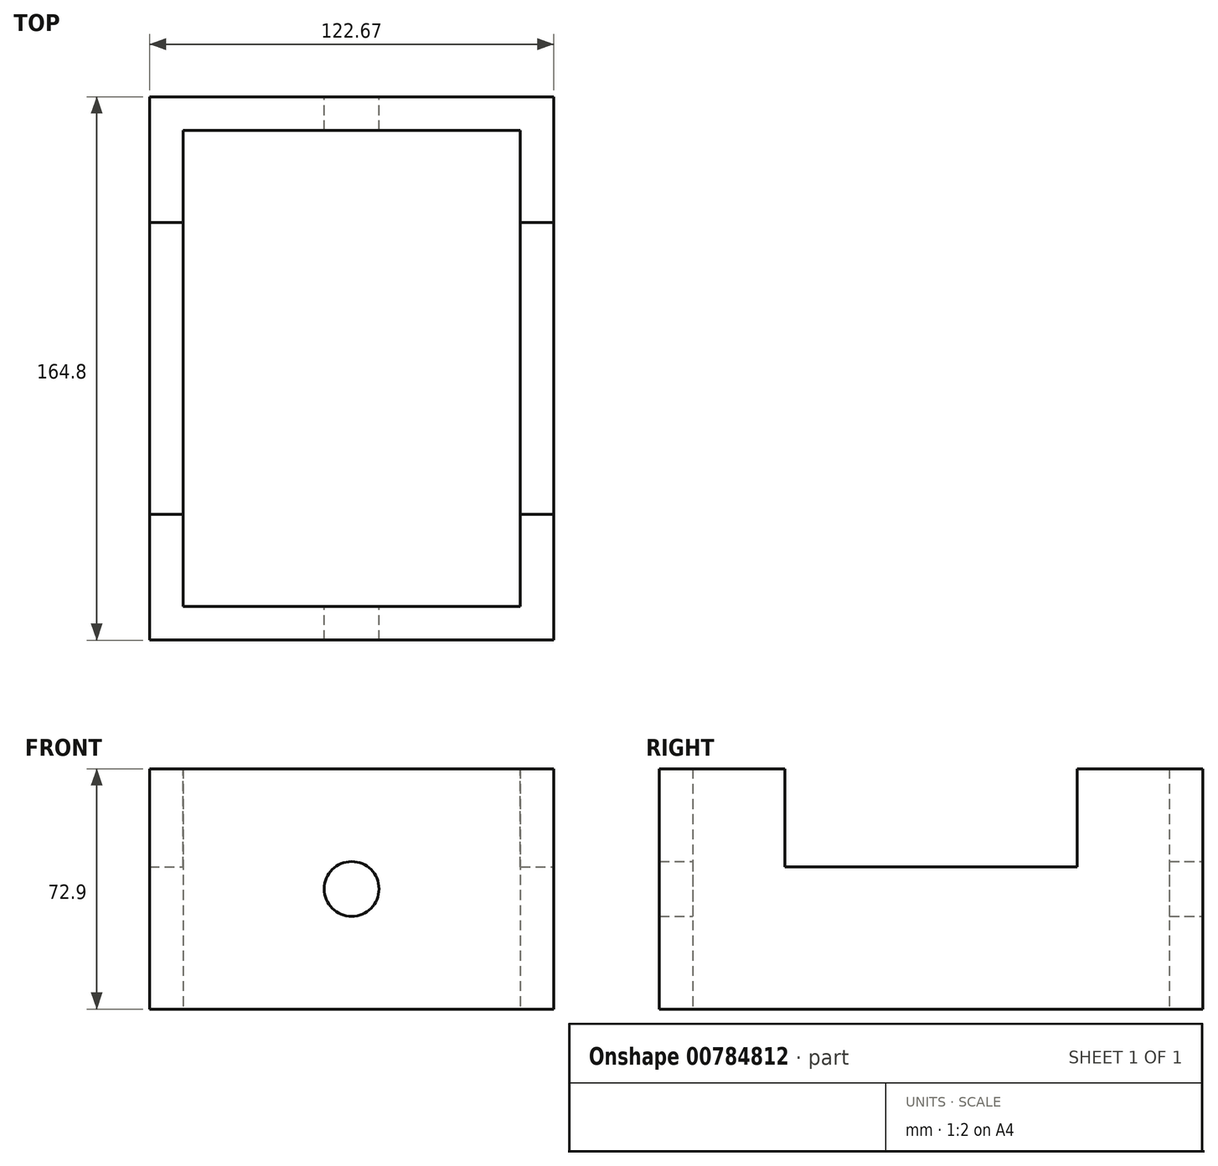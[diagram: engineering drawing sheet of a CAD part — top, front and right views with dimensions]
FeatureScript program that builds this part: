
annotation { "Feature Type Name" : "Feature", "Feature Type Description" : "" }
export const myFeature = defineFeature(function(context is Context, id is Id, definition is map)
    precondition{}
    {
        {
            var Q0;
            Q0=qCreatedBy(makeId("Top.planeOp"),FACE);
            var sketch = newSketch(context, id + "F0", { "sketchPlane" : qUnion([Q0])});
            skLineSegment(sketch, "E0.bottom", {"start": v(-84.1, 82.4) * mm, "end": v(38.56, 82.4) * mm});
            skLineSegment(sketch, "E0.top", {"start": v(-84.1, -82.4) * mm, "end": v(38.56, -82.4) * mm});
            skLineSegment(sketch, "E0.left", {"start": v(-84.1, 82.4) * mm, "end": v(-84.1, -82.4) * mm});
            skLineSegment(sketch, "E0.right", {"start": v(38.56, 82.4) * mm, "end": v(38.56, -82.4) * mm});
            skLineSegment(sketch, "E1.bottom", {"start": v(-73.95, 72.24) * mm, "end": v(28.4, 72.24) * mm});
            skLineSegment(sketch, "E1.top", {"start": v(-73.95, -72.24) * mm, "end": v(28.4, -72.24) * mm});
            skLineSegment(sketch, "E1.left", {"start": v(-73.95, 72.24) * mm, "end": v(-73.95, -72.24) * mm});
            skLineSegment(sketch, "E1.right", {"start": v(28.4, 72.24) * mm, "end": v(28.4, -72.24) * mm});
            skSolve(sketch);
        }
        {
            var Q0;
            Q0=makeQuery(id+"F0.imprint","IMPRINT",FACE,{"disambiguationData":[TD([[makeQuery(id+"F0.imprint","IMPRINT",EDGE,{"derivedFrom":sQuery(id+"F0.wireOp",EDGE,"E0.bottom")}),-1.0]])]});
            extrude(context, id + "F1", {"entities" : qUnion([Q0]), "depth" : 72.9 * mm, "offsetDistance" : 25.4 * mm});
        }
        {
            var Q0;
            Q0=makeQuery(id+"F1.opExtrude","SWEPT_FACE",FACE,{"disambiguationData":[OSD([sQuery(id+"F0.wireOp",EDGE,"E0.bottom")])]});
            var sketch = newSketch(context, id + "F2", { "sketchPlane" : qUnion([Q0])});
            skCircle(sketch, "E2", {"center": v(22.78, 36.45) * mm, "radius": 8.3 * mm});
            skPoint(sketch, "E2.centerSnap0", {"position": v(84.1, 36.45) * mm});
            skPoint(sketch, "E2.centerSnap1", {"position": v(22.78, 72.9) * mm});
            skSolve(sketch);
        }
        {
            var Q0;
            Q0=makeQuery(id+"F2.imprint","IMPRINT",FACE,{"disambiguationData":[TD([[makeQuery(id+"F2.imprint","IMPRINT",EDGE,{"derivedFrom":sQuery(id+"F2.wireOp",EDGE,"E2")}),1.0]])]});
            extrude(context, id + "F3", {"entities" : qUnion([Q0]), "operationType" : NewBodyOperationType.REMOVE, "oppositeDirection" : true, "depth" : 244.1 * mm, "offsetDistance" : 25.4 * mm});
        }
        {
            var Q0;
            Q0=makeQuery(id+"F1.opExtrude","CAP_FACE",FACE,{"disambiguationData":[OSD([sQuery(id+"F0.wireOp",EDGE,"E0.bottom"),sQuery(id+"F0.wireOp",EDGE,"E0.top"),sQuery(id+"F0.wireOp",EDGE,"E0.left"),sQuery(id+"F0.wireOp",EDGE,"E0.right"),sQuery(id+"F0.wireOp",EDGE,"E1.bottom"),sQuery(id+"F0.wireOp",EDGE,"E1.top"),sQuery(id+"F0.wireOp",EDGE,"E1.left"),sQuery(id+"F0.wireOp",EDGE,"E1.right")])],"isStart":false});
            var sketch = newSketch(context, id + "F4", { "sketchPlane" : qUnion([Q0])});
            skLineSegment(sketch, "E3", {"start": v(-84.1, 44.3) * mm, "end": v(-73.95, 44.3) * mm});
            skLineSegment(sketch, "E4", {"start": v(-84.1, -44.3) * mm, "end": v(-73.95, -44.3) * mm});
            skLineSegment(sketch, "E5", {"start": v(28.4, 44.3) * mm, "end": v(38.56, 44.3) * mm});
            skLineSegment(sketch, "E6", {"start": v(28.4, -44.3) * mm, "end": v(38.56, -44.3) * mm});
            skSolve(sketch);
        }
        {
            var Q0;
            {var subQ0=sQuery(id+"F4.wireOp",EDGE,"E5");Q0=makeQuery(id+"F4.imprint","IMPRINT",FACE,{"disambiguationData":[TD([[makeQuery(id+"F4.imprint","IMPRINT",EDGE,{"derivedFrom":subQ0}),-1.0]])]});}
            var Q1;
            {var subQ0=sQuery(id+"F4.wireOp",EDGE,"E3");Q1=makeQuery(id+"F4.imprint","IMPRINT",FACE,{"disambiguationData":[TD([[makeQuery(id+"F4.imprint","IMPRINT",EDGE,{"derivedFrom":subQ0}),-1.0]])]});}
            extrude(context, id + "F5", {"entities" : qUnion([Q0, Q1]), "operationType" : NewBodyOperationType.REMOVE, "oppositeDirection" : true, "depth" : 29.72 * mm, "offsetDistance" : 25.4 * mm});
        }
    });
